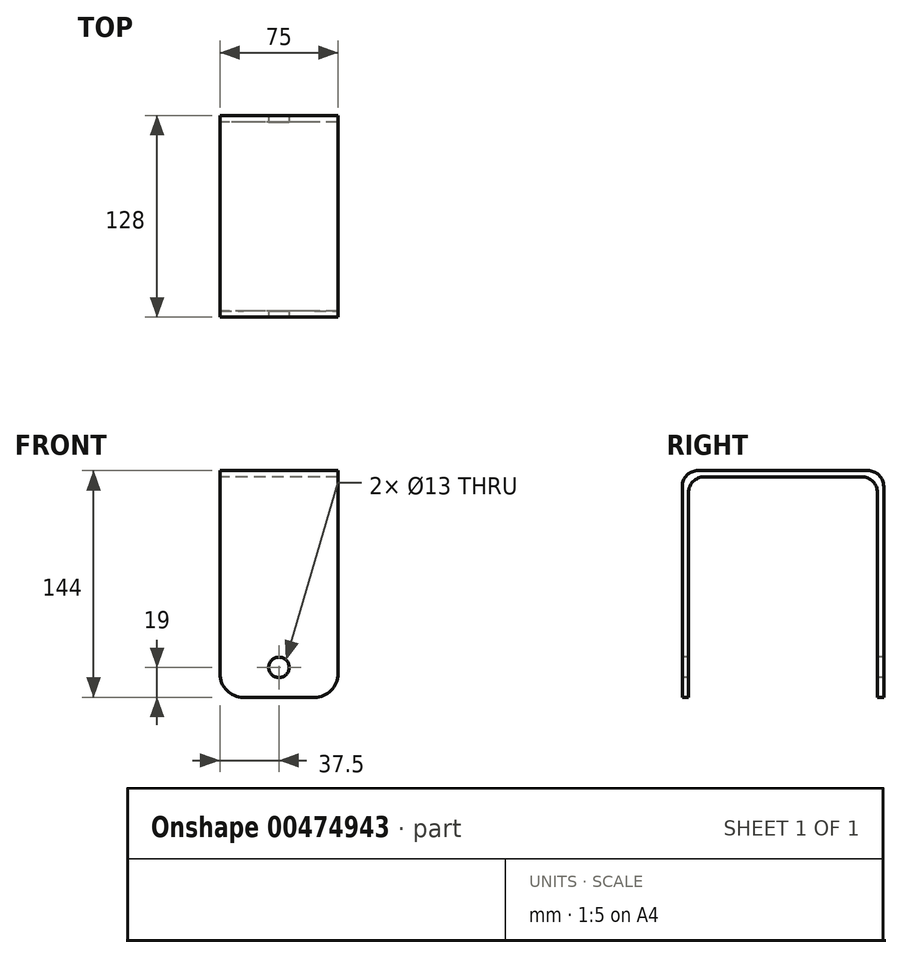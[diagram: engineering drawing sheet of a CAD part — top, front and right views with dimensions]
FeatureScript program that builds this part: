
annotation { "Feature Type Name" : "Feature", "Feature Type Description" : "" }
export const myFeature = defineFeature(function(context is Context, id is Id, definition is map)
    precondition{}
    {
        {
            var Q0;
            Q0=qCreatedBy(makeId("Right.planeOp"),FACE);
            var sketch = newSketch(context, id + "F0", { "sketchPlane" : qUnion([Q0])});
            skLineSegment(sketch, "E0", {"start": v(-64, 0) * mm, "end": v(-64, 134) * mm});
            skLineSegment(sketch, "E1", {"start": v(-54, 144) * mm, "end": v(54, 144) * mm});
            skLineSegment(sketch, "E2", {"start": v(64, 134) * mm, "end": v(64, 0) * mm});
            skLineSegment(sketch, "E3", {"start": v(-64, 0) * mm, "end": v(-60, 0) * mm});
            skLineSegment(sketch, "E4", {"start": v(-60, 0) * mm, "end": v(-60, 130) * mm});
            skLineSegment(sketch, "E5", {"start": v(-50, 140) * mm, "end": v(50, 140) * mm});
            skLineSegment(sketch, "E6", {"start": v(60, 130) * mm, "end": v(60, 0) * mm});
            skLineSegment(sketch, "E7", {"start": v(60, 0) * mm, "end": v(64, 0) * mm});
            skPoint(sketch, "E8.visualSharp", {"position": v(-60, 140) * mm});
            skArc(sketch, "E8.filletArc", {"start": v(-50, 140) * mm, "mid": v(-57.07, 137.07) * mm, "end": v(-60, 130) * mm});
            skPoint(sketch, "E9.visualSharp", {"position": v(60, 140) * mm});
            skArc(sketch, "E9.filletArc", {"start": v(60, 130) * mm, "mid": v(57.07, 137.07) * mm, "end": v(50, 140) * mm});
            skPoint(sketch, "E10.visualSharp", {"position": v(64, 144) * mm});
            skArc(sketch, "E10.filletArc", {"start": v(64, 134) * mm, "mid": v(61.07, 141.07) * mm, "end": v(54, 144) * mm});
            skPoint(sketch, "E11.visualSharp", {"position": v(-64, 144) * mm});
            skArc(sketch, "E11.filletArc", {"start": v(-54, 144) * mm, "mid": v(-61.07, 141.07) * mm, "end": v(-64, 134) * mm});
            skSolve(sketch);
        }
        {
            var Q0;
            Q0 = qSketchRegion(id + "F0", true);
            extrude(context, id + "F1", {"entities" : qUnion([Q0]), "depth" : 75 * mm});
        }
        {
            var Q0;
            Q0=makeQuery(id+"F1.opExtrude","SWEPT_FACE",FACE,{"disambiguationData":[OSD([sQuery(id+"F0.wireOp",EDGE,"E0")])]});
            var sketch = newSketch(context, id + "F2", { "sketchPlane" : qUnion([Q0])});
            skCircle(sketch, "E12", {"center": v(37.5, 19) * mm, "radius": 6.5 * mm});
            skSolve(sketch);
        }
        {
            var Q0;
            Q0=sQuery(id+"F2.wireOp",VERTEX,"E12.center");
            var Q1;
            Q1=makeQuery(id+"F1.opExtrude","SWEPT_BODY",BODY,{"disambiguationData":[OSD([sQuery(id+"F0.wireOp",EDGE,"E0"),sQuery(id+"F0.wireOp",EDGE,"E1"),sQuery(id+"F0.wireOp",EDGE,"E2"),sQuery(id+"F0.wireOp",EDGE,"E3"),sQuery(id+"F0.wireOp",EDGE,"E4"),sQuery(id+"F0.wireOp",EDGE,"E5"),sQuery(id+"F0.wireOp",EDGE,"E6"),sQuery(id+"F0.wireOp",EDGE,"E7"),sQuery(id+"F0.wireOp",EDGE,"E8.filletArc"),sQuery(id+"F0.wireOp",EDGE,"E9.filletArc"),sQuery(id+"F0.wireOp",EDGE,"E10.filletArc"),sQuery(id+"F0.wireOp",EDGE,"E11.filletArc")])]});
            hole(context, id + "F3", {"style" : HoleStyle.SIMPLE, "endStyle" : HoleEndStyle.BLIND, "holeDiameter" : 13 * mm, "holeDepth" : 500 * mm, "isTappedThrough" : true, "tappedDepth" : 12 * mm, "tapClearance" : 3, "locations" : qUnion([Q0]), "scope" : qUnion([Q1])});
        }
        {
            var Q0;
            Q0=makeQuery(id+"F1.opExtrude","CAP_EDGE",EDGE,{"disambiguationData":[OSD([sQuery(id+"F0.wireOp",EDGE,"E3")])],"isStart":true});
            var Q1;
            Q1=makeQuery(id+"F1.opExtrude","CAP_EDGE",EDGE,{"disambiguationData":[OSD([sQuery(id+"F0.wireOp",EDGE,"E3")])],"isStart":false});
            var Q2;
            Q2=makeQuery(id+"F1.opExtrude","CAP_EDGE",EDGE,{"disambiguationData":[OSD([sQuery(id+"F0.wireOp",EDGE,"E7")])],"isStart":false});
            var Q3;
            Q3=makeQuery(id+"F1.opExtrude","CAP_EDGE",EDGE,{"disambiguationData":[OSD([sQuery(id+"F0.wireOp",EDGE,"E7")])],"isStart":true});
            fillet(context, id + "F4", {"entities" : qUnion([Q0, Q1, Q2, Q3]), "radius" : 15 * mm, "tangentPropagation" : true, "allowEdgeOverflow" : false});
        }
    });
